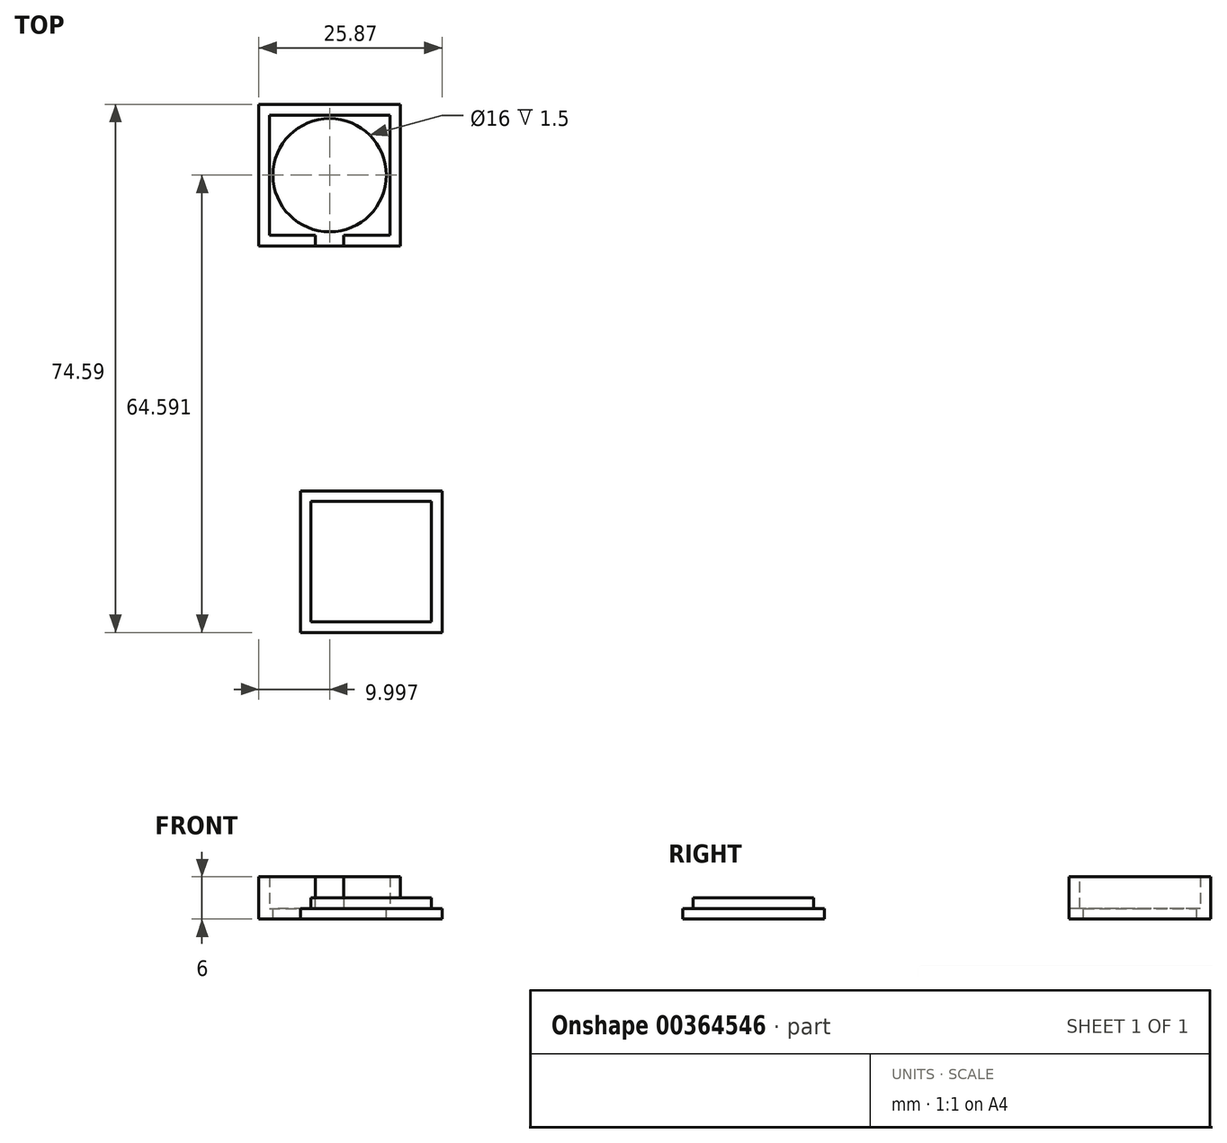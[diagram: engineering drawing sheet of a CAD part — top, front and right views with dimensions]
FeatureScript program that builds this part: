
annotation { "Feature Type Name" : "Feature", "Feature Type Description" : "" }
export const myFeature = defineFeature(function(context is Context, id is Id, definition is map)
    precondition{}
    {
        {
            var Q0;
            Q0=qCreatedBy(makeId("Top.planeOp"),FACE);
            var sketch = newSketch(context, id + "F0", { "sketchPlane" : qUnion([Q0])});
            skLineSegment(sketch, "E0.bottom", {"start": v(21.1, -15.83) * mm, "end": v(41.1, -15.83) * mm});
            skLineSegment(sketch, "E0.top", {"start": v(21.1, -35.83) * mm, "end": v(41.1, -35.83) * mm});
            skLineSegment(sketch, "E0.left", {"start": v(21.1, -15.83) * mm, "end": v(21.1, -35.83) * mm});
            skLineSegment(sketch, "E0.right", {"start": v(41.1, -15.83) * mm, "end": v(41.1, -35.83) * mm});
            skLineSegment(sketch, "E1.bottom", {"start": v(46.98, -70.42) * mm, "end": v(26.98, -70.42) * mm});
            skLineSegment(sketch, "E1.top", {"start": v(46.98, -90.42) * mm, "end": v(26.98, -90.42) * mm});
            skLineSegment(sketch, "E1.left", {"start": v(46.98, -70.42) * mm, "end": v(46.98, -90.42) * mm});
            skLineSegment(sketch, "E1.right", {"start": v(26.98, -70.42) * mm, "end": v(26.98, -90.42) * mm});
            skLineSegment(sketch, "E2.0", {"start": v(45.48, -71.92) * mm, "end": v(28.48, -71.92) * mm});
            skLineSegment(sketch, "E2.1", {"start": v(45.48, -71.92) * mm, "end": v(45.48, -88.92) * mm});
            skLineSegment(sketch, "E2.2", {"start": v(45.48, -88.92) * mm, "end": v(28.48, -88.92) * mm});
            skLineSegment(sketch, "E2.3", {"start": v(28.48, -71.92) * mm, "end": v(28.48, -88.92) * mm});
            skLineSegment(sketch, "E3", {"start": v(28.48, -88.92) * mm, "end": v(28.48, -83.92) * mm});
            skLineSegment(sketch, "E4", {"start": v(28.48, -83.92) * mm, "end": v(33.48, -83.92) * mm, "construction": true});
            skSolve(sketch);
        }
        {
            var Q0;
            Q0=makeQuery(id+"F0.imprint","IMPRINT",FACE,{"disambiguationData":[TD([[makeQuery(id+"F0.imprint","IMPRINT",EDGE,{"derivedFrom":sQuery(id+"F0.wireOp",EDGE,"E0.bottom")}),-1.0]])]});
            extrude(context, id + "F1", {"entities" : qUnion([Q0]), "depth" : 6 * mm});
        }
        {
            var Q0;
            Q0=makeQuery(id+"F1.opExtrude","CAP_FACE",FACE,{"disambiguationData":[OSD([sQuery(id+"F0.wireOp",EDGE,"E0.bottom"),sQuery(id+"F0.wireOp",EDGE,"E0.top"),sQuery(id+"F0.wireOp",EDGE,"E0.left"),sQuery(id+"F0.wireOp",EDGE,"E0.right")])],"isStart":false});
            shell(context, id + "F2", {"entities" : qUnion([Q0]), "thickness" : 1.5 * mm});
        }
        {
            var Q0;
            Q0=makeQuery(id+"F2.opShell","OFFSET_FACE",FACE,{"disambiguationData":[OSD([sQuery(id+"F0.wireOp",EDGE,"E0.bottom"),sQuery(id+"F0.wireOp",EDGE,"E0.top"),sQuery(id+"F0.wireOp",EDGE,"E0.left"),sQuery(id+"F0.wireOp",EDGE,"E0.right")])]});
            var sketch = newSketch(context, id + "F3", { "sketchPlane" : qUnion([Q0])});
            skLineSegment(sketch, "E5.0", {"start": v(39.6, -17.33) * mm, "end": v(39.6, -34.33) * mm});
            skLineSegment(sketch, "E6.0", {"start": v(22.6, -34.33) * mm, "end": v(39.6, -34.33) * mm});
            skLineSegment(sketch, "E7.0", {"start": v(22.6, -17.33) * mm, "end": v(39.6, -17.33) * mm});
            skLineSegment(sketch, "E8.0", {"start": v(22.6, -17.33) * mm, "end": v(22.6, -34.33) * mm});
            skCircle(sketch, "E9", {"center": v(31.1, -25.83) * mm, "radius": 8 * mm});
            skPoint(sketch, "E9.centerSnap0", {"position": v(39.6, -25.83) * mm});
            skPoint(sketch, "E9.centerSnap1", {"position": v(31.1, -17.33) * mm});
            skSolve(sketch);
        }
        {
            var Q0;
            Q0=makeQuery(id+"F3.imprint","IMPRINT",FACE,{"disambiguationData":[TD([[makeQuery(id+"F3.imprint","IMPRINT",EDGE,{"derivedFrom":sQuery(id+"F3.wireOp",EDGE,"E9")}),1.0]])]});
            extrude(context, id + "F4", {"entities" : qUnion([Q0]), "operationType" : NewBodyOperationType.REMOVE, "endBound" : BoundingType.UP_TO_NEXT, "oppositeDirection" : true, "depth" : 25 * mm});
        }
        {
            var Q0;
            Q0=makeQuery(id+"F0.imprint","IMPRINT",FACE,{"disambiguationData":[TD([[makeQuery(id+"F0.imprint","IMPRINT",EDGE,{"derivedFrom":sQuery(id+"F0.wireOp",EDGE,"E1.bottom")}),1.0]])]});
            var Q1;
            Q1=makeQuery(id+"F0.imprint","IMPRINT",FACE,{"disambiguationData":[TD([[makeQuery(id+"F0.imprint","IMPRINT",EDGE,{"derivedFrom":sQuery(id+"F0.wireOp",EDGE,"E2.0")}),1.0]])]});
            extrude(context, id + "F5", {"entities" : qUnion([Q0, Q1]), "depth" : 1.5 * mm});
        }
        {
            var Q0;
            Q0=makeQuery(id+"F0.imprint","IMPRINT",FACE,{"disambiguationData":[TD([[makeQuery(id+"F0.imprint","IMPRINT",EDGE,{"derivedFrom":sQuery(id+"F0.wireOp",EDGE,"E2.0")}),1.0]])]});
            extrude(context, id + "F6", {"entities" : qUnion([Q0]), "operationType" : NewBodyOperationType.ADD, "depth" : 3 * mm});
        }
        {
            var Q0;
            Q0=makeQuery(id+"F1.opExtrude","SWEPT_FACE",FACE,{"disambiguationData":[OSD([sQuery(id+"F0.wireOp",EDGE,"E0.top")])]});
            var sketch = newSketch(context, id + "F7", { "sketchPlane" : qUnion([Q0])});
            skLineSegment(sketch, "E10", {"start": v(21.1, 0) * mm, "end": v(29.1, 0) * mm});
            skLineSegment(sketch, "E11", {"start": v(29.1, 0) * mm, "end": v(29.1, 1.5) * mm});
            skLineSegment(sketch, "E12", {"start": v(29.1, 1.5) * mm, "end": v(29.1, 6) * mm});
            skLineSegment(sketch, "E13", {"start": v(29.1, 6) * mm, "end": v(33.1, 6) * mm});
            skLineSegment(sketch, "E14", {"start": v(33.1, 6) * mm, "end": v(33.1, 1.5) * mm});
            skLineSegment(sketch, "E15", {"start": v(33.1, 1.5) * mm, "end": v(29.1, 1.5) * mm});
            skSolve(sketch);
        }
        {
            var Q0;
            Q0=makeQuery(id+"F7.imprint","IMPRINT",FACE,{"disambiguationData":[TD([[makeQuery(id+"F7.imprint","IMPRINT",EDGE,{"derivedFrom":sQuery(id+"F7.wireOp",EDGE,"E12")}),-1.0]])]});
            extrude(context, id + "F8", {"entities" : qUnion([Q0]), "operationType" : NewBodyOperationType.REMOVE, "endBound" : BoundingType.UP_TO_NEXT, "oppositeDirection" : true, "depth" : 25 * mm});
        }
    });
